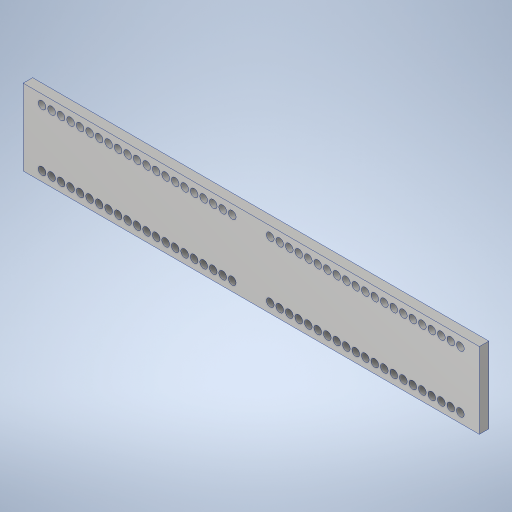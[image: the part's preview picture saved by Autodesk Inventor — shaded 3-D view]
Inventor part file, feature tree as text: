
AUTODESK INVENTOR PART (.ipt)
format: ipt  version: 2023.4 (Build 274418000, 418)  size: 340,992 bytes
history: native  units: in
note: dims shown in document units (in); Inventor stores cm internally (conversion verified against a paired STEP export)
features: sketch x2, extrude x1, hole x1
ambient origin geometry x8: Origin, YZ Plane, XZ Plane, XY Plane, X Axis, Y Axis, Z Axis, Center Point
bodies: Solid1 (feature_tree)
feature tree (4):
  extrude  "Extrusion1"  Depth=2.0in
  hole  "Hole1"  [1 undecoded]
  sketch  "Sketch1"  dims[d0=12.0in d1=2.0in]
  sketch  "Sketch2"  dims[d2=0.25in d3=0.0in d4=0.5in d5=0.25in d6=8.2677in d8=0.25in d9=0.3937in d11=1.0in d13=0.25in d14=0.201in d15=0.75in d16=0.385in d17=0.25in d18=0.5635in d19=1.0in d20=0.8108in]
note: 1 required parameter value undecoded (feature->parameter linkage not recoverable at this tier; creation-order binding heuristic only, values carry confidence <= 0.55)
